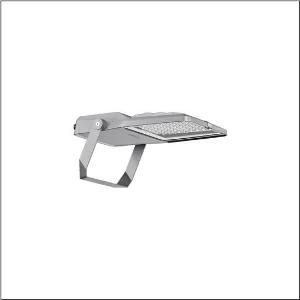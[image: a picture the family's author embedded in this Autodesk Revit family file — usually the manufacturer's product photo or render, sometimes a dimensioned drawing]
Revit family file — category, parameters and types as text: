
# Revit family: floodlight_fl_21_iq_mini___rs12_5xa7772d2b1a_9233
name_source: partatom
category: Lighting Fixtures
units: mm (PartAtom-declared; Revit-internal decimal feet)

## family parameters
Cut with Voids When Loaded = No
Host = Face
Light Source = No
Part Type = Normal
Room Calculation Point = No
Round Connector Dimension = Use Diameter
Shared = No

## types (1)
- --- (1 x LED, 18020 lm, 143 W, 3000K)
    Apparent Load = 143 VA
    CIE Flux Codes = 79 92 99 100 100
    Color Rendering = 70
    Color Temperature = 3000K
    Default Elevation = 1800 mm
    Description = Floodlight FL 21 iQ mini, floodlight, primary light control with lens, of PMMA, primary optical cover: protective disc, of toughened safety glass, transparent, light distribution: RS12, light emission: direct distribution, installation type: surface-mounted, LED, High Power LED, rated luminous flux: 18.020lm, luminous efficacy: 126lm/W, light colour: 730, colour temperature: 3000K, control: Street-Remote, Auto-Match, Temp-Guard, Night-Set, Smart-Wire, Desk-Remote (wireless, voltage-free reading and setting of iQ features in the workshop via application-optimized NFC function/RFID function), optimised constant luminous flux control (CLO 2.0), with terminal, 6-pole, mains connection: 220..240V, AC, 50/60Hz, start of lifetime: 143W, end of service life: 152W, reduction: 61W, luminaire housing, of diecast aluminium, powder-coated, Siteco® metallic grey (DB 702S), corrosivity category C5 mid according to DIN EN ISO 12944, sealing non-destructively replaceable, mounting bracket, of steel, galvanised, powder-coated, Siteco® metallic grey (DB 702S), protection rating (complete): IP66, insulation class (complete): insulation class II (safety insulation), certification: CE, ENEC, VDE, protection symbol: D, impact resistance: IK08, permissible operating ambient temperature: -40..+40°C, permissible operating ambient temperature for outdoor applications: -40..+50°C, standard: DIN EN 12944, LABS conformity tested according to VDMA 24364:2018-05, packaging unit: 1 piece

Light Distribution: RS12
    Height = 70 mm
    Lamp = 1 x LED
    Lamp Light Flux = 18020 lm
    Lamp Power = 143 W
    Lamp count = 1
    Length = 485 mm
    Luminous efficacy = 126 lm/W
    Manufacturer = Siteco
    ModVariant = No
    Model = 5XA7772D2B1A
    Number of Poles = 1
    OnlyDefault = Yes
    Power Factor = 1
    Product Name = Floodlight FL 21 iQ mini | RS12
    Product group = floodlight | pylon annexe
    ProductGroupID = 6200
    Protection Class = Protection class II
    Protection Degree = IP 66
    RLX_Detail_Level = 1
    RLX_Emergency_Light_Flux = 0 lm
    RLX_Emergency_Type = 0
    RLX_Emergency_Type_DB = No
    RlxData = <blob elided: 91221 chars, md5=b0c0b132>
    Socket = socket
    Standby Power = 0 W
    System Light Flux = 18020 lm
    System Power = 143 W
    Type Comments = factory setting: luminous flux: 100 % | dim-lin: 254 | 730 mA
    Type Image = l_1006845.jpg
    URL = http://relux.com
    VarID = @adj_117543
    Voltage = 0 V
    Weight = 0.00 kg
    Width = 337 mm

## geometry (parser evidence)
native form markers: Blend x4, Sweep x14
no freeform markers — native parametric forms only
